# Revit family: RUSHWORK_400_DN40-600
name_source: partatom
category: Арматура трубопроводов
units: mm (PartAtom-declared; Revit-internal decimal feet)

## family parameters
Всегда вертикально = Нет
На основе рабочей плоскости = Нет
Общий = Нет
При загрузке вырезать с полостями = Нет
Размер круглого соединителя = Использовать диаметр
Тип детали = Клапан - Вставляется

## types (15) — shared parameters
ADSK_Единица измерения = шт
ADSK_Завод-изготовитель = ООО ТД "РАШВОРК"
URL = https://rwru.ru
Изготовитель = ООО ТД "РАШВОРК"
Материал корпус = чугун GJL-250 (GG25)
zero-valued in all types: Отметка по умолчанию

## per-type parameters (varying)
| type | ADSK_Код изделия | ADSK_Масса | ADSK_Наименование | ADSK_Наименование краткое | D_Eвыдавливания | D_Hвыдавливания | D_Конектор | D_клапана | F штока | L_клапана | Высота штока | Н-L_выдавливание | Н_выдавливание | Направление потока | Ц |
| Клапан обратный двухстворчатый РАШВОРК® 400-040-16, DN040, PN16, корпус - GJL-250 (GG25), диск - CF8M (AISI316), уплотнение - EPDM, М/Ф | 400-040-16 | 1.2 | Клапан обратный двухстворчатый РАШВОРК® 400-040-16, DN040, PN16, корпус - GJL-250 (GG25), диск - CF8M (AISI316), уплотнение - EPDM, М/Ф | Клапан обратный двухстворчатый РАШВОРК®, DN040, PN16 | 45 мм | 57 мм | 40 мм | 85 мм | 15 мм | 17 мм | 70 мм | 18 мм | 15 мм | 95 мм | 168 мм |
| Клапан обратный двухстворчатый РАШВОРК® 400-050-16, DN050, PN16, корпус - GJL-250 (GG25), диск - CF8M (AISI316), уплотнение - EPDM, М/Ф | 400-050-16 | 1.5 | Клапан обратный двухстворчатый РАШВОРК® 400-050-16, DN050, PN16, корпус - GJL-250 (GG25), диск - CF8M (AISI316), уплотнение - EPDM, М/Фратный двухстворчатый РАШВОРК® 400-040-16, DN040, PN16, корпус - GJL-250 (GG25), диск - CF8M (AISI316), уплотнение - EPDM, М/Ф | Клапан обратный двухстворчатый РАШВОРК®, DN050, PN16 | 45 мм | 66 мм | 50 мм | 101 мм | 15 мм | 27 мм | 86 мм | 39 мм | 15 мм | 111 мм | 168 мм |
| Клапан обратный двухстворчатый РАШВОРК® 400-065-16, DN065, PN16, корпус - GJL-250 (GG25), диск - CF8M (AISI316), уплотнение - EPDM, М/Ф | 400-065-16 | 2 | Клапан обратный двухстворчатый РАШВОРК® 400-065-16, DN065, PN16, корпус - GJL-250 (GG25), диск - CF8M (AISI316), уплотнение - EPDM, М/Ф | Клапан обратный двухстворчатый РАШВОРК®, DN065, PN16 | 59 мм | 80 мм | 65 мм | 119 мм | 17 мм | 27 мм | 104 мм | 37 мм | 17 мм | 129 мм | 168 мм |
| Клапан обратный двухстворчатый РАШВОРК® 400-080-16, DN080, PN16, корпус - GJL-250 (GG25), диск - CF8M (AISI316), уплотнение - EPDM, М/Ф | 400-080-16 | 2.6 | Клапан обратный двухстворчатый РАШВОРК® 400-080-16, DN080, PN16, корпус - GJL-250 (GG25), диск - CF8M (AISI316), уплотнение - EPDM, М/Ф | Клапан обратный двухстворчатый РАШВОРК®, DN080, PN16 | 72 мм | 95 мм | 80 мм | 133 мм | 19 мм | 29 мм | 118 мм | 38 мм | 19 мм | 143 мм | 168 мм |
| Клапан обратный двухстворчатый РАШВОРК® 400-100-16, DN100, PN16, корпус - GJL-250 (GG25), диск - CF8M (AISI316), уплотнение - EPDM, М/Ф | 400-100-16 | 4.1 | Клапан обратный двухстворчатый РАШВОРК® 400-100-16, DN100, PN16, корпус - GJL-250 (GG25), диск - CF8M (AISI316), уплотнение - EPDM, М/Ф | Клапан обратный двухстворчатый РАШВОРК®, DN100, PN16 | 90 мм | 117 мм | 100 мм | 164 мм | 23 мм | 32 мм | 149 мм | 41 мм | 23 мм | 174 мм | 168 мм |
| Клапан обратный двухстворчатый РАШВОРК® 400-125-16, DN125, PN16, корпус - GJL-250 (GG25), диск - CF8M (AISI316), уплотнение - EPDM, М/Ф | 400-125-16 | 6.4 | Клапан обратный двухстворчатый РАШВОРК® 400-125-16, DN125, PN16, корпус - GJL-250 (GG25), диск - CF8M (AISI316), уплотнение - EPDM, М/Ф | Клапан обратный двухстворчатый РАШВОРК®, DN125, PN16 | 110 мм | 145 мм | 125 мм | 194 мм | 26 мм | 35 мм | 179 мм | 44 мм | 26 мм | 204 мм | 168 мм |
| Клапан обратный двухстворчатый РАШВОРК® 400-150-16, DN150, PN16, корпус - GJL-250 (GG25), диск - CF8M (AISI316), уплотнение - EPDM, М/Ф | 400-150-16 | 7.8 | Клапан обратный двухстворчатый РАШВОРК® 400-150-16, DN150, PN16, корпус - GJL-250 (GG25), диск - CF8M (AISI316), уплотнение - EPDM, М/Ф | Клапан обратный двухстворчатый РАШВОРК®, DN150, PN16 | 135 мм | 170 мм | 150 мм | 220 мм | 28 мм | 38 мм | 205 мм | 48 мм | 28 мм | 230 мм | 168 мм |
| Клапан обратный двухстворчатый РАШВОРК® 400-200-16, DN200, PN16, корпус - GJL-250 (GG25), диск - CF8M (AISI316), уплотнение - EPDM, М/Ф | 400-200-16 | 16.1 | Клапан обратный двухстворчатый РАШВОРК® 400-200-16, DN200, PN16, корпус - GJL-250 (GG25), диск - CF8M (AISI316), уплотнение - EPDM, М/Ф | Клапан обратный двухстворчатый РАШВОРК®, DN200, PN16 | 175 мм | 224 мм | 200 мм | 275 мм | 38 мм | 48 мм | 260 мм | 57 мм | 38 мм | 285 мм | 168 мм |
| Клапан обратный двухстворчатый РАШВОРК® 400-250-16, DN250, PN16, корпус - GJL-250 (GG25), диск - CF8M (AISI316), уплотнение - EPDM, М/Ф | 400-250-16 | 25.1 | Клапан обратный двухстворчатый РАШВОРК® 400-250-16, DN250, PN16, корпус - GJL-250 (GG25), диск - CF8M (AISI316), уплотнение - EPDM, М/Ф | Клапан обратный двухстворчатый РАШВОРК®, DN250, PN16 | 215 мм | 255 мм | 250 мм | 328 мм | 43 мм | 53 мм | 313 мм | 62 мм | 43 мм | 338 мм | 168 мм |
| Клапан обратный двухстворчатый РАШВОРК® 400-300-16, DN300, PN16, корпус - GJL-250 (GG25), диск - CF8M (AISI316), уплотнение - EPDM, М/Ф | 400-300-16 | 33.9 | Клапан обратный двухстворчатый РАШВОРК® 400-300-16, DN300, PN16, корпус - GJL-250 (GG25), диск - CF8M (AISI316), уплотнение - EPDM, М/Ф | Клапан обратный двухстворчатый РАШВОРК®, DN300, PN16 | 224 мм | 302 мм | 300 мм | 378 мм | 50 мм | 72 мм | 363 мм | 93 мм | 50 мм | 388 мм | 168 мм |
| Клапан обратный двухстворчатый РАШВОРК® 400-350-16, DN350, PN16, корпус - GJL-250 (GG25), диск - CF8M (AISI316), уплотнение - EPDM, М/Ф | 400-350-16 | 55 | Клапан обратный двухстворчатый РАШВОРК® 400-350-16, DN350, PN16, корпус - GJL-250 (GG25), диск - CF8M (AISI316), уплотнение - EPDM, М/Ф | Клапан обратный двухстворчатый РАШВОРК®, DN350, PN16 | 236 мм | 348 мм | 350 мм | 440 мм | 57 мм | 64 мм | 425 мм | 70 мм | 57 мм | 450 мм | 0 мм |
| Клапан обратный двухстворчатый РАШВОРК® 400-400-16, DN400, PN16, корпус - GJL-250 (GG25), диск - CF8M (AISI316), уплотнение - EPDM, М/Ф | 400-400-16 | 73 | Клапан обратный двухстворчатый РАШВОРК® 400-400-16, DN400, PN16, корпус - GJL-250 (GG25), диск - CF8M (AISI316), уплотнение - EPDM, М/Ф | Клапан обратный двухстворчатый РАШВОРК®, DN400, PN16 | 248 мм | 403 мм | 400 мм | 491 мм | 62 мм | 70 мм | 476 мм | 80 мм | 60 мм | 501 мм | 168 мм |
| Клапан обратный двухстворчатый РАШВОРК® 400-450-16, DN450, PN16, корпус - GJL-250 (GG25), диск - CF8M (AISI316), уплотнение - EPDM, М/Ф | 400-450-16 | 99 | Клапан обратный двухстворчатый РАШВОРК® 400-450-16, DN450, PN16, корпус - GJL-250 (GG25), диск - CF8M (AISI316), уплотнение - EPDM, М/Ф | Клапан обратный двухстворчатый РАШВОРК®, DN450, PN16 | 260 мм | 446 мм | 450 мм | 541 мм | 67 мм | 76 мм | 526 мм | 88 мм | 64 мм | 551 мм | 168 мм |
| Клапан обратный двухстворчатый РАШВОРК® 400-500-16, DN500, PN16, корпус - GJL-250 (GG25), диск - CF8M (AISI316), уплотнение - EPDM, М/Ф | 400-500-16 | 117 | Клапан обратный двухстворчатый РАШВОРК® 400-500-16, DN500, PN16, корпус - GJL-250 (GG25), диск - CF8M (AISI316), уплотнение - EPDM, М/Ф | Клапан обратный двухстворчатый РАШВОРК®, DN500, PN16 | 272 мм | 490 мм | 500 мм | 544 мм | 69 мм | 76 мм | 529 мм | 82 мм | 70 мм | 554 мм | 168 мм |
| Клапан обратный двухстворчатый РАШВОРК® 400-600-16, DN600, PN16, корпус - GJL-250 (GG25), диск - CF8M (AISI316), уплотнение - EPDM, М/Ф | 400-600-16 | 215 | Клапан обратный двухстворчатый РАШВОРК® 400-600-16, DN600, PN16, корпус - GJL-250 (GG25), диск - CF8M (AISI316), уплотнение - EPDM, М/Ф | Клапан обратный двухстворчатый РАШВОРК®, DN600, PN16 | 284 мм | 520 мм | 600 мм | 696 мм | 72 мм | 89 мм | 681 мм | 99 мм | 79 мм | 706 мм | 168 мм |

## geometry (parser evidence)
native form markers: Blend x2
no freeform markers — native parametric forms only
